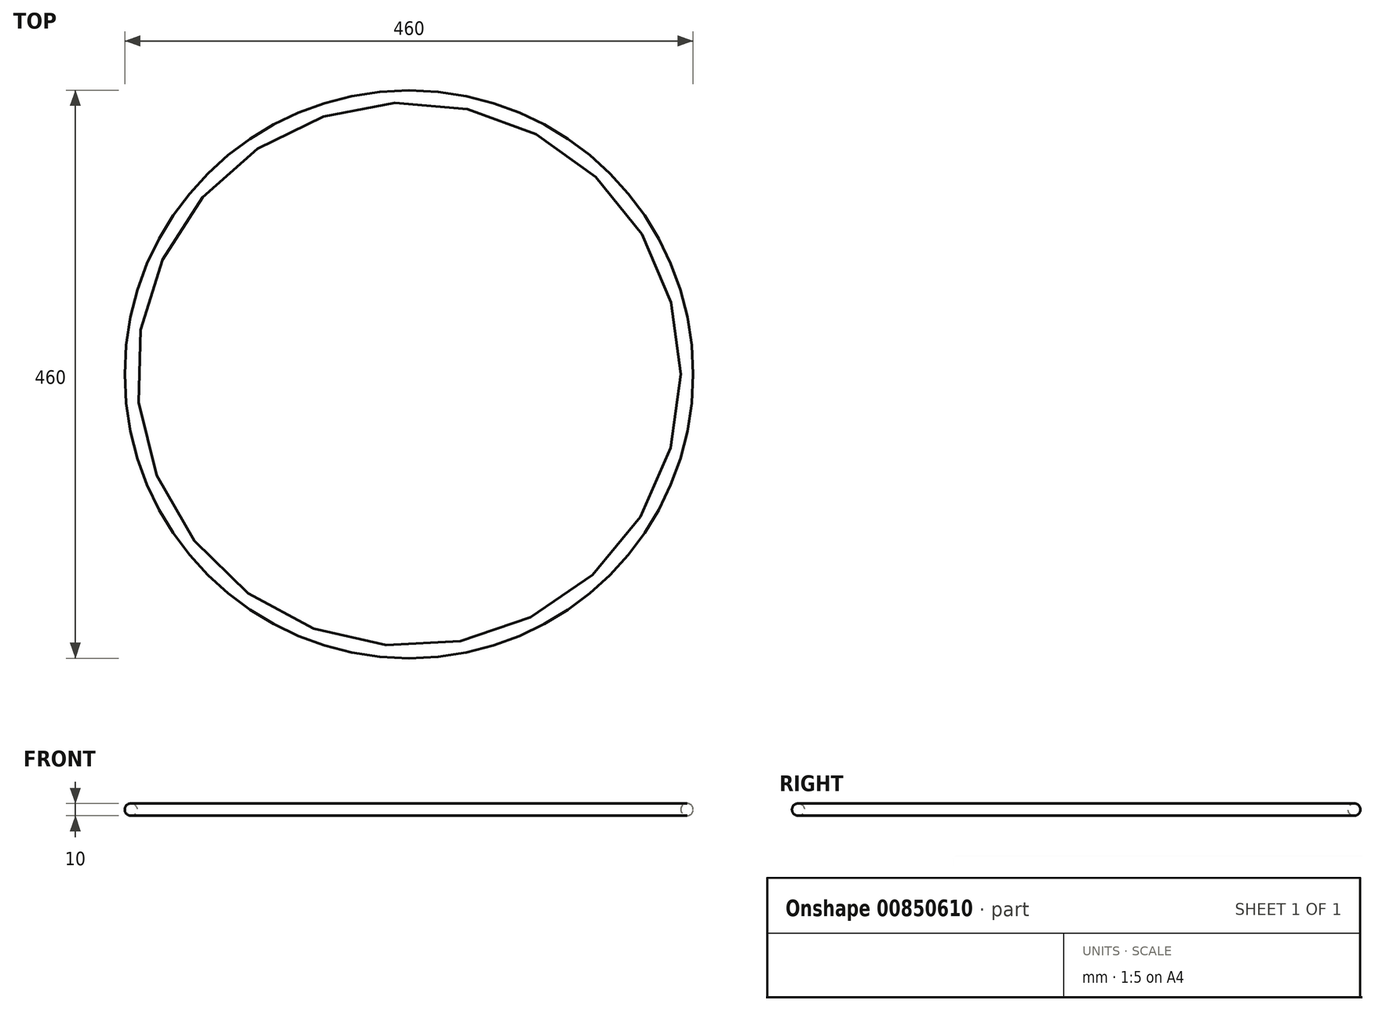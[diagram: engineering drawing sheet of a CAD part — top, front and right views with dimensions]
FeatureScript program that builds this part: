
annotation { "Feature Type Name" : "Feature", "Feature Type Description" : "" }
export const myFeature = defineFeature(function(context is Context, id is Id, definition is map)
    precondition{}
    {
        {
            var Q0;
            Q0=qCreatedBy(makeId("Front.planeOp"),FACE);
            var sketch = newSketch(context, id + "F0", { "sketchPlane" : qUnion([Q0])});
            skLineSegment(sketch, "E0", {"start": v(0, 40.15) * mm, "end": v(0, -41.03) * mm});
            skCircle(sketch, "E1", {"center": v(225, 2.77) * mm, "radius": 5 * mm});
            skSolve(sketch);
        }
        {
            var Q0;
            Q0=makeQuery(id+"F0.imprint","IMPRINT",FACE,{"disambiguationData":[TD([[makeQuery(id+"F0.imprint","IMPRINT",EDGE,{"derivedFrom":sQuery(id+"F0.wireOp",EDGE,"E1")}),1.0]])]});
            var Q1;
            Q1=sQuery(id+"F0.wireOp",EDGE,"E0");
            revolve(context, id + "F1", {"surfaceOperationType" : NewSurfaceOperationType.NEW, "entities" : qUnion([Q0]), "axis" : qUnion([Q1]), "revolveType" : RevolveType.FULL});
        }
    });
